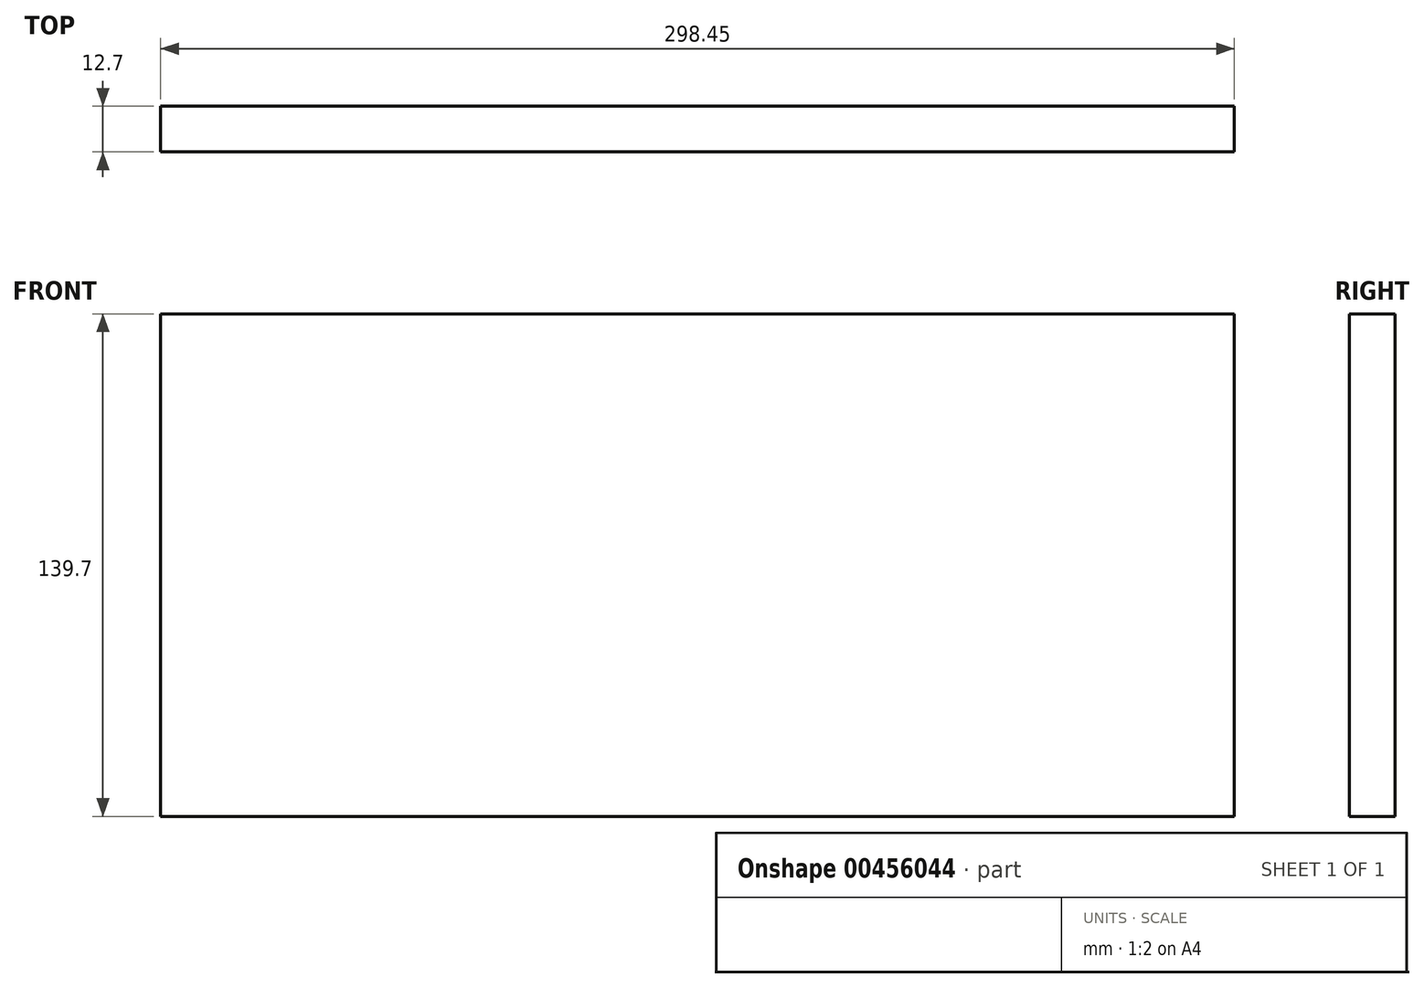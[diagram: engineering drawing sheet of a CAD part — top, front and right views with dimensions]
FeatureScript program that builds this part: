
annotation { "Feature Type Name" : "Feature", "Feature Type Description" : "" }
export const myFeature = defineFeature(function(context is Context, id is Id, definition is map)
    precondition{}
    {
        {
            var Q0;
            Q0=qCreatedBy(makeId("Front.planeOp"),FACE);
            var sketch = newSketch(context, id + "F0", { "sketchPlane" : qUnion([Q0])});
            skLineSegment(sketch, "E0.bottom", {"start": v(0, 0) * mm, "end": v(-298.45, 0) * mm});
            skLineSegment(sketch, "E0.top", {"start": v(0, 139.7) * mm, "end": v(-298.45, 139.7) * mm});
            skLineSegment(sketch, "E0.left", {"start": v(0, 0) * mm, "end": v(0, 139.7) * mm});
            skLineSegment(sketch, "E0.right", {"start": v(-298.45, 0) * mm, "end": v(-298.45, 139.7) * mm});
            skSolve(sketch);
        }
        {
            var Q0;
            Q0=makeQuery(id+"F0.imprint","IMPRINT",FACE,{"disambiguationData":[TD([[makeQuery(id+"F0.imprint","IMPRINT",EDGE,{"derivedFrom":sQuery(id+"F0.wireOp",EDGE,"E0.bottom")}),-1.0]])]});
            extrude(context, id + "F1", {"entities" : qUnion([Q0]), "depth" : 12.7 * mm});
        }
    });
